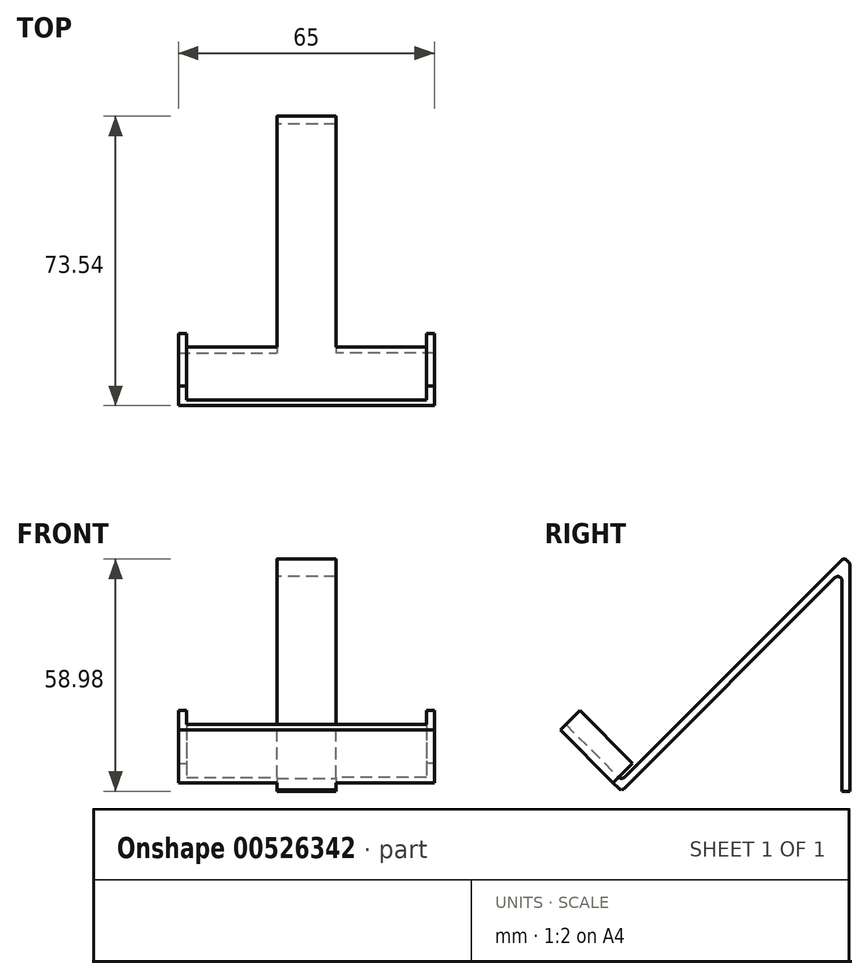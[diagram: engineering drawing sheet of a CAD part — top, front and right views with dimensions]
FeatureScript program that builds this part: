
annotation { "Feature Type Name" : "Feature", "Feature Type Description" : "" }
export const myFeature = defineFeature(function(context is Context, id is Id, definition is map)
    precondition{}
    {
        {
            var Q0;
            Q0=qCreatedBy(makeId("Right.planeOp"),FACE);
            var sketch = newSketch(context, id + "F0", { "sketchPlane" : qUnion([Q0])});
            skLineSegment(sketch, "E0", {"start": v(-39.03, -28.87) * mm, "end": v(-24.89, -43.01) * mm});
            skLineSegment(sketch, "E1", {"start": v(-24.89, -43.01) * mm, "end": v(31.68, 13.56) * mm});
            skLineSegment(sketch, "E2.0", {"start": v(-24.89, -45.84) * mm, "end": v(31.1, 10.14) * mm});
            skLineSegment(sketch, "E2.1", {"start": v(-40.44, -30.28) * mm, "end": v(-24.89, -45.84) * mm});
            skLineSegment(sketch, "E3", {"start": v(-39.03, -28.87) * mm, "end": v(-40.44, -30.28) * mm});
            skLineSegment(sketch, "E4", {"start": v(31.68, 13.56) * mm, "end": v(33.1, 12.14) * mm});
            skLineSegment(sketch, "E5", {"start": v(33.1, 12.14) * mm, "end": v(33.1, -45.84) * mm});
            skLineSegment(sketch, "E6", {"start": v(31.1, -45.84) * mm, "end": v(31.1, 10.14) * mm});
            skLineSegment(sketch, "E7", {"start": v(33.1, -45.84) * mm, "end": v(31.1, -45.84) * mm});
            skSolve(sketch);
        }
        {
            var Q0;
            Q0=makeQuery(id+"F0.imprint","IMPRINT",FACE,{"disambiguationData":[TD([[makeQuery(id+"F0.imprint","IMPRINT",EDGE,{"derivedFrom":sQuery(id+"F0.wireOp",EDGE,"E0")}),-1.0]])]});
            extrude(context, id + "F1", {"entities" : qUnion([Q0]), "depth" : 15 * mm, "offsetDistance" : 25 * mm});
        }
        {
            var Q0;
            Q0=makeQuery(id+"F1.opExtrude","SWEPT_EDGE",EDGE,{"disambiguationData":[OSD([sQuery(id+"F0.wireOp",EDGE,"E0"),sQuery(id+"F0.wireOp",EDGE,"E1")])]});
            fillet(context, id + "F2", {"entities" : qUnion([Q0]), "radius" : 1 * mm, "tangentPropagation" : true, "allowEdgeOverflow" : false});
        }
        {
            var Q0;
            Q0=makeQuery(id+"F1.opExtrude","SWEPT_EDGE",EDGE,{"disambiguationData":[OSD([sQuery(id+"F0.wireOp",EDGE,"E2.0"),sQuery(id+"F0.wireOp",EDGE,"E6")])]});
            fillet(context, id + "F3", {"entities" : qUnion([Q0]), "radius" : 1 * mm, "tangentPropagation" : true, "allowEdgeOverflow" : false});
        }
        {
            var Q0;
            Q0=makeQuery(id+"F1.opExtrude","SWEPT_EDGE",EDGE,{"disambiguationData":[OSD([sQuery(id+"F0.wireOp",EDGE,"E2.0"),sQuery(id+"F0.wireOp",EDGE,"E2.1")])]});
            var Q1;
            Q1=makeQuery(id+"F1.opExtrude","SWEPT_EDGE",EDGE,{"disambiguationData":[OSD([sQuery(id+"F0.wireOp",EDGE,"E1"),sQuery(id+"F0.wireOp",EDGE,"E4")])]});
            var Q2;
            Q2=makeQuery(id+"F1.opExtrude","SWEPT_EDGE",EDGE,{"disambiguationData":[OSD([sQuery(id+"F0.wireOp",EDGE,"E4"),sQuery(id+"F0.wireOp",EDGE,"E5")])]});
            fillet(context, id + "F4", {"entities" : qUnion([Q0, Q1, Q2]), "radius" : 1 * mm, "tangentPropagation" : true, "allowEdgeOverflow" : false});
        }
        {
            var Q0;
            Q0=makeQuery(id+"F1.opExtrude","CAP_FACE",FACE,{"disambiguationData":[OSD([sQuery(id+"F0.wireOp",EDGE,"E0"),sQuery(id+"F0.wireOp",EDGE,"E1"),sQuery(id+"F0.wireOp",EDGE,"E2.0"),sQuery(id+"F0.wireOp",EDGE,"E2.1"),sQuery(id+"F0.wireOp",EDGE,"E3"),sQuery(id+"F0.wireOp",EDGE,"E4"),sQuery(id+"F0.wireOp",EDGE,"E5"),sQuery(id+"F0.wireOp",EDGE,"E6"),sQuery(id+"F0.wireOp",EDGE,"E7")])],"isStart":false});
            var sketch = newSketch(context, id + "F5", { "sketchPlane" : qUnion([Q0])});
            skLineSegment(sketch, "E8.0", {"start": v(-39.03, -28.87) * mm, "end": v(-25.6, -42.3) * mm});
            skLineSegment(sketch, "E9", {"start": v(-25.6, -42.3) * mm, "end": v(-27, -43.72) * mm});
            skLineSegment(sketch, "E10", {"start": v(-27, -43.72) * mm, "end": v(-40.44, -30.28) * mm});
            skLineSegment(sketch, "E11", {"start": v(-40.44, -30.28) * mm, "end": v(-39.03, -28.87) * mm});
            skSolve(sketch);
        }
        {
            var Q0;
            Q0 = qSketchRegion(id + "F5", true);
            extrude(context, id + "F6", {"entities" : qUnion([Q0]), "operationType" : NewBodyOperationType.ADD, "depth" : 25 * mm, "offsetDistance" : 25 * mm});
        }
        {
            var Q0;
            Q0=makeQuery(id+"F1.opExtrude","CAP_FACE",FACE,{"disambiguationData":[OSD([sQuery(id+"F0.wireOp",EDGE,"E0"),sQuery(id+"F0.wireOp",EDGE,"E1"),sQuery(id+"F0.wireOp",EDGE,"E2.0"),sQuery(id+"F0.wireOp",EDGE,"E2.1"),sQuery(id+"F0.wireOp",EDGE,"E3"),sQuery(id+"F0.wireOp",EDGE,"E4"),sQuery(id+"F0.wireOp",EDGE,"E5"),sQuery(id+"F0.wireOp",EDGE,"E6"),sQuery(id+"F0.wireOp",EDGE,"E7")])],"isStart":true});
            var sketch = newSketch(context, id + "F7", { "sketchPlane" : qUnion([Q0])});
            skLineSegment(sketch, "E12.0", {"start": v(39.03, -28.87) * mm, "end": v(25.6, -42.3) * mm});
            skLineSegment(sketch, "E13.0", {"start": v(39.03, -28.87) * mm, "end": v(40.44, -30.28) * mm});
            skLineSegment(sketch, "E14", {"start": v(25.6, -42.3) * mm, "end": v(27, -43.72) * mm});
            skLineSegment(sketch, "E15", {"start": v(27, -43.72) * mm, "end": v(40.44, -30.28) * mm});
            skSolve(sketch);
        }
        {
            var Q0;
            Q0 = qSketchRegion(id + "F7", true);
            extrude(context, id + "F8", {"entities" : qUnion([Q0]), "operationType" : NewBodyOperationType.ADD, "depth" : 25 * mm, "offsetDistance" : 25 * mm});
        }
        {
            var Q0;
            Q0=makeQuery(id+"F8.boolean.opBoolean","MERGE",FACE,{"derivedFrom":[makeQuery(id+"F6.boolean.opBoolean","MERGE",FACE,{"derivedFrom":[makeQuery(id+"F1.opExtrude","SWEPT_FACE",FACE,{"disambiguationData":[OSD([sQuery(id+"F0.wireOp",EDGE,"E0")])]}),makeQuery(id+"F6.opExtrude","SWEPT_FACE",FACE,{"disambiguationData":[OSD([sQuery(id+"F5.wireOp",EDGE,"E8.0")])]})]}),makeQuery(id+"F8.opExtrude","SWEPT_FACE",FACE,{"disambiguationData":[OSD([sQuery(id+"F7.wireOp",EDGE,"E12.0")])]})]});
            var sketch = newSketch(context, id + "F9", { "sketchPlane" : qUnion([Q0])});
            skLineSegment(sketch, "E16.bottom", {"start": v(25, 7.18) * mm, "end": v(23, 7.18) * mm});
            skLineSegment(sketch, "E16.top", {"start": v(25, -11.82) * mm, "end": v(23, -11.82) * mm});
            skLineSegment(sketch, "E16.left", {"start": v(25, 7.18) * mm, "end": v(25, -11.82) * mm});
            skLineSegment(sketch, "E16.right", {"start": v(23, 7.18) * mm, "end": v(23, -11.82) * mm});
            skLineSegment(sketch, "E17.bottom", {"start": v(-40, 7.18) * mm, "end": v(-38, 7.18) * mm});
            skLineSegment(sketch, "E17.top", {"start": v(-40, -11.82) * mm, "end": v(-38, -11.82) * mm});
            skLineSegment(sketch, "E17.left", {"start": v(-40, 7.18) * mm, "end": v(-40, -11.82) * mm});
            skLineSegment(sketch, "E17.right", {"start": v(-38, 7.18) * mm, "end": v(-38, -11.82) * mm});
            skSolve(sketch);
        }
        {
            var Q0;
            Q0=makeQuery(id+"F9.imprint","IMPRINT",FACE,{"disambiguationData":[TD([[makeQuery(id+"F9.imprint","IMPRINT",EDGE,{"derivedFrom":sQuery(id+"F9.wireOp",EDGE,"E16.bottom")}),-1.0]])]});
            var Q1;
            Q1=makeQuery(id+"F9.imprint","IMPRINT",FACE,{"disambiguationData":[TD([[makeQuery(id+"F9.imprint","IMPRINT",EDGE,{"derivedFrom":sQuery(id+"F9.wireOp",EDGE,"E17.bottom")}),-1.0]])]});
            extrude(context, id + "F10", {"entities" : qUnion([Q0, Q1]), "operationType" : NewBodyOperationType.ADD, "depth" : 5 * mm, "offsetDistance" : 25 * mm});
        }
    });
